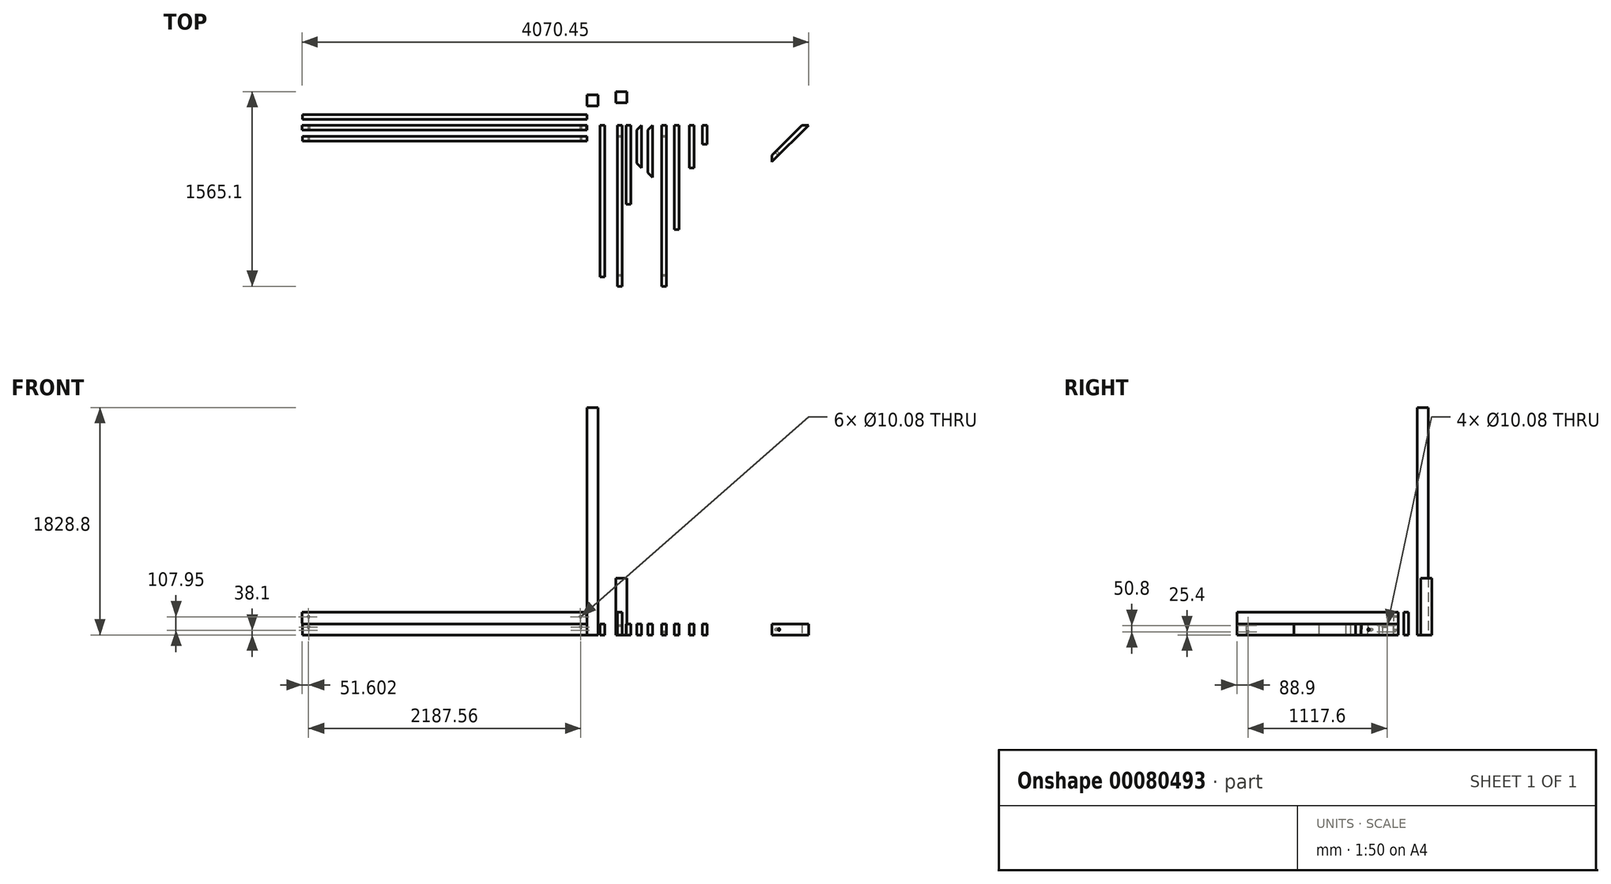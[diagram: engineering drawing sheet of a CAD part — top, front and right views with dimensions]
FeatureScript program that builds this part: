
annotation { "Feature Type Name" : "Feature", "Feature Type Description" : "" }
export const myFeature = defineFeature(function(context is Context, id is Id, definition is map)
    precondition{}
    {
        {
            var Q0;
            Q0=qCreatedBy(makeId("Right.planeOp"),FACE);
            var sketch = newSketch(context, id + "F0", { "sketchPlane" : qUnion([Q0])});
            skLineSegment(sketch, "E0.bottom", {"start": v(0, 0) * mm, "end": v(-38.1, 0) * mm});
            skLineSegment(sketch, "E0.top", {"start": v(0, 184.15) * mm, "end": v(-38.1, 184.15) * mm});
            skLineSegment(sketch, "E0.left", {"start": v(0, 0) * mm, "end": v(0, 184.15) * mm});
            skLineSegment(sketch, "E0.right", {"start": v(-38.1, 0) * mm, "end": v(-38.1, 184.15) * mm});
            skSolve(sketch);
        }
        {
            var Q0;
            Q0=makeQuery(id+"F0.imprint","IMPRINT",FACE,{"disambiguationData":[TD([[makeQuery(id+"F0.imprint","IMPRINT",EDGE,{"derivedFrom":sQuery(id+"F0.wireOp",EDGE,"E0.bottom")}),-1.0]])]});
            extrude(context, id + "F1", {"entities" : qUnion([Q0]), "oppositeDirection" : true, "depth" : 2289.96 * mm});
        }
        {
            var Q0;
            Q0=makeQuery(id+"F1.opExtrude","SWEPT_FACE",FACE,{"disambiguationData":[OSD([sQuery(id+"F0.wireOp",EDGE,"E0.right")])]});
            var sketch = newSketch(context, id + "F2", { "sketchPlane" : qUnion([Q0])});
            skLineSegment(sketch, "E1", {"start": v(0, 0) * mm, "end": v(0, 184.15) * mm});
            skLineSegment(sketch, "E2", {"start": v(0, 184.15) * mm, "end": v(-3.84, 184.15) * mm});
            skLineSegment(sketch, "E3", {"start": v(-3.84, 184.15) * mm, "end": v(0, 0) * mm});
            skLineSegment(sketch, "E4", {"start": v(-2289.96, 184.15) * mm, "end": v(-2286.13, 0) * mm});
            skLineSegment(sketch, "E5", {"start": v(-2286.13, 0) * mm, "end": v(-2289.96, 0) * mm});
            skLineSegment(sketch, "E6", {"start": v(-2289.96, 0) * mm, "end": v(-2289.96, 184.15) * mm});
            skSolve(sketch);
        }
        {
            var Q0;
            Q0 = qSketchRegion(id + "F2", true);
            extrude(context, id + "F3", {"entities" : qUnion([Q0]), "operationType" : NewBodyOperationType.REMOVE, "oppositeDirection" : true, "depth" : 38.1 * mm});
        }
        {
            var Q0;
            Q0=qCreatedBy(makeId("Front.planeOp"),FACE);
            var sketch = newSketch(context, id + "F4", { "sketchPlane" : qUnion([Q0])});
            skLineSegment(sketch, "E7.bottom", {"start": v(103.6, 0) * mm, "end": v(141.7, 0) * mm});
            skLineSegment(sketch, "E7.top", {"start": v(103.6, 88.9) * mm, "end": v(141.7, 88.9) * mm});
            skLineSegment(sketch, "E7.left", {"start": v(103.6, 0) * mm, "end": v(103.6, 88.9) * mm});
            skLineSegment(sketch, "E7.right", {"start": v(141.7, 0) * mm, "end": v(141.7, 88.9) * mm});
            skSolve(sketch);
        }
        {
            var Q0;
            Q0=makeQuery(id+"F4.imprint","IMPRINT",FACE,{"disambiguationData":[TD([[makeQuery(id+"F4.imprint","IMPRINT",EDGE,{"derivedFrom":sQuery(id+"F4.wireOp",EDGE,"E7.bottom")}),1.0]])]});
            extrude(context, id + "F5", {"entities" : qUnion([Q0]), "depth" : 1219.2 * mm});
        }
        {
            var Q0;
            Q0=qCreatedBy(makeId("Top.planeOp"),FACE);
            var sketch = newSketch(context, id + "F6", { "sketchPlane" : qUnion([Q0])});
            skLineSegment(sketch, "E8.bottom", {"start": v(0, 155.1) * mm, "end": v(88.9, 155.1) * mm});
            skLineSegment(sketch, "E8.top", {"start": v(0, 244) * mm, "end": v(88.9, 244) * mm});
            skLineSegment(sketch, "E8.left", {"start": v(0, 155.1) * mm, "end": v(0, 244) * mm});
            skLineSegment(sketch, "E8.right", {"start": v(88.9, 155.1) * mm, "end": v(88.9, 244) * mm});
            skSolve(sketch);
        }
        {
            var Q0;
            Q0 = qSketchRegion(id + "F6", true);
            extrude(context, id + "F7", {"entities" : qUnion([Q0]), "depth" : 1828.8 * mm});
        }
        {
            var Q0;
            Q0=qCreatedBy(makeId("Front.planeOp"),FACE);
            var sketch = newSketch(context, id + "F8", { "sketchPlane" : qUnion([Q0])});
            skLineSegment(sketch, "E9.bottom", {"start": v(244.55, 0) * mm, "end": v(282.65, 0) * mm});
            skLineSegment(sketch, "E9.top", {"start": v(244.55, 184.15) * mm, "end": v(282.65, 184.15) * mm});
            skLineSegment(sketch, "E9.left", {"start": v(244.55, 0) * mm, "end": v(244.55, 184.15) * mm});
            skLineSegment(sketch, "E9.right", {"start": v(282.65, 0) * mm, "end": v(282.65, 184.15) * mm});
            skSolve(sketch);
        }
        {
            var Q0;
            Q0=makeQuery(id+"F8.imprint","IMPRINT",FACE,{"disambiguationData":[TD([[makeQuery(id+"F8.imprint","IMPRINT",EDGE,{"derivedFrom":sQuery(id+"F8.wireOp",EDGE,"E9.bottom")}),1.0]])]});
            extrude(context, id + "F9", {"entities" : qUnion([Q0]), "depth" : 1295.4 * mm});
        }
        {
            var Q0;
            Q0=qCreatedBy(makeId("Front.planeOp"),FACE);
            var sketch = newSketch(context, id + "F10", { "sketchPlane" : qUnion([Q0])});
            skLineSegment(sketch, "E10.bottom", {"start": v(312.63, 0) * mm, "end": v(350.73, 0) * mm});
            skLineSegment(sketch, "E10.top", {"start": v(312.63, 88.9) * mm, "end": v(350.73, 88.9) * mm});
            skLineSegment(sketch, "E10.left", {"start": v(312.63, 0) * mm, "end": v(312.63, 88.9) * mm});
            skLineSegment(sketch, "E10.right", {"start": v(350.73, 0) * mm, "end": v(350.73, 88.9) * mm});
            skSolve(sketch);
        }
        {
            var Q0;
            Q0=makeQuery(id+"F10.imprint","IMPRINT",FACE,{"disambiguationData":[TD([[makeQuery(id+"F10.imprint","IMPRINT",EDGE,{"derivedFrom":sQuery(id+"F10.wireOp",EDGE,"E10.bottom")}),1.0]])]});
            extrude(context, id + "F11", {"entities" : qUnion([Q0]), "depth" : 635 * mm});
        }
        {
            var Q0;
            Q0=makeQuery(id+"F1.opExtrude","SWEPT_FACE",FACE,{"disambiguationData":[OSD([sQuery(id+"F0.wireOp",EDGE,"E0.right")])]});
            var sketch = newSketch(context, id + "F12", { "sketchPlane" : qUnion([Q0])});
            skPoint(sketch, "E11", {"position": v(-2238.36, 146.05) * mm});
            skPoint(sketch, "E12", {"position": v(-2236.1, 38.1) * mm});
            skPoint(sketch, "E13", {"position": v(-53.85, 146.05) * mm});
            skPoint(sketch, "E14", {"position": v(-51.6, 38.1) * mm});
            skSolve(sketch);
        }
        {
            var Q0;
            Q0=sQuery(id+"F12.wireOp",VERTEX,"E14");
            var Q1;
            Q1=sQuery(id+"F12.wireOp",VERTEX,"E13");
            var Q2;
            Q2=sQuery(id+"F12.wireOp",VERTEX,"E12");
            var Q3;
            Q3=sQuery(id+"F12.wireOp",VERTEX,"E11");
            var Q4;
            Q4=makeQuery(id+"F1.opExtrude","SWEPT_BODY",BODY,{"disambiguationData":[OSD([sQuery(id+"F0.wireOp",EDGE,"E0.bottom"),sQuery(id+"F0.wireOp",EDGE,"E0.top"),sQuery(id+"F0.wireOp",EDGE,"E0.left"),sQuery(id+"F0.wireOp",EDGE,"E0.right")])]});
            hole(context, id + "F13", {"style" : HoleStyle.SIMPLE, "endStyle" : HoleEndStyle.THROUGH, "standardTappedOrClearance" : lookupTablePath({ "standard" : "ANSI", "fit" : "Normal (ASME)", "size" : "3/8", "type" : "Clearance" }), "standardBlindInLast" : lookupTablePath({ "fit" : "Free", "standard" : "ANSI", "size" : "3/8", "type" : "Clearance" }), "holeDiameter" : 10.08 * mm, "locations" : qUnion([Q0, Q1, Q2, Q3]), "scope" : qUnion([Q4]), "isTappedThrough" : true});
        }
        {
            var Q0;
            Q0=makeQuery(id+"F9.opExtrude","SWEPT_FACE",FACE,{"disambiguationData":[OSD([sQuery(id+"F8.wireOp",EDGE,"E9.right")])]});
            var sketch = newSketch(context, id + "F14", { "sketchPlane" : qUnion([Q0])});
            skPoint(sketch, "E15", {"position": v(-1206.5, 76.2) * mm});
            skPoint(sketch, "E16", {"position": v(-88.9, 76.2) * mm});
            skSolve(sketch);
        }
        {
            var Q0;
            Q0=sQuery(id+"F14.wireOp",VERTEX,"4c446d8b-93f8-499f-88b7-25f558c8394a");
            var Q1;
            Q1=sQuery(id+"F14.wireOp",VERTEX,"E15");
            var Q2;
            Q2=sQuery(id+"F14.wireOp",VERTEX,"E16");
            var Q3;
            Q3=sQuery(id+"F14.wireOp",VERTEX,"ef1d34a0-cfd4-4a64-a352-8786edb42035");
            var Q4;
            Q4=makeQuery(id+"F9.opExtrude","SWEPT_BODY",BODY,{"disambiguationData":[OSD([sQuery(id+"F8.wireOp",EDGE,"E9.bottom"),sQuery(id+"F8.wireOp",EDGE,"E9.top"),sQuery(id+"F8.wireOp",EDGE,"E9.left"),sQuery(id+"F8.wireOp",EDGE,"E9.right")])]});
            hole(context, id + "F15", {"style" : HoleStyle.SIMPLE, "endStyle" : HoleEndStyle.THROUGH, "standardTappedOrClearance" : lookupTablePath({ "standard" : "ANSI", "fit" : "Normal (ASME)", "size" : "3/8", "type" : "Clearance" }), "standardBlindInLast" : lookupTablePath({ "fit" : "Free", "standard" : "ANSI", "size" : "3/8", "type" : "Clearance" }), "holeDiameter" : 10.08 * mm, "locations" : qUnion([Q0, Q1, Q2, Q3]), "scope" : qUnion([Q4]), "isTappedThrough" : true});
        }
        {
            var Q0;
            Q0=qCreatedBy(makeId("Front.planeOp"),FACE);
            var sketch = newSketch(context, id + "F16", { "sketchPlane" : qUnion([Q0])});
            skLineSegment(sketch, "E17.bottom", {"start": v(399.52, 0) * mm, "end": v(437.62, 0) * mm});
            skLineSegment(sketch, "E17.top", {"start": v(399.52, 88.9) * mm, "end": v(437.62, 88.9) * mm});
            skLineSegment(sketch, "E17.left", {"start": v(399.52, 0) * mm, "end": v(399.52, 88.9) * mm});
            skLineSegment(sketch, "E17.right", {"start": v(437.62, 0) * mm, "end": v(437.62, 88.9) * mm});
            skSolve(sketch);
        }
        {
            var Q0;
            Q0=makeQuery(id+"F16.imprint","IMPRINT",FACE,{"disambiguationData":[TD([[makeQuery(id+"F16.imprint","IMPRINT",EDGE,{"derivedFrom":sQuery(id+"F16.wireOp",EDGE,"E17.bottom")}),1.0]])]});
            extrude(context, id + "F17", {"entities" : qUnion([Q0]), "depth" : 342.9 * mm});
        }
        {
            var Q0;
            Q0=makeQuery(id+"F17.opExtrude","SWEPT_FACE",FACE,{"disambiguationData":[OSD([sQuery(id+"F16.wireOp",EDGE,"E17.top")])]});
            var sketch = newSketch(context, id + "F18", { "sketchPlane" : qUnion([Q0])});
            skLineSegment(sketch, "E18", {"start": v(437.62, 0) * mm, "end": v(399.52, -38.1) * mm});
            skLineSegment(sketch, "E19", {"start": v(399.52, -38.1) * mm, "end": v(399.52, 0) * mm});
            skLineSegment(sketch, "E20", {"start": v(399.52, 0) * mm, "end": v(437.62, 0) * mm});
            skLineSegment(sketch, "E21", {"start": v(437.62, -342.9) * mm, "end": v(399.52, -304.8) * mm});
            skLineSegment(sketch, "E22", {"start": v(399.52, -304.8) * mm, "end": v(399.52, -342.9) * mm});
            skLineSegment(sketch, "E23", {"start": v(399.52, -342.9) * mm, "end": v(437.62, -342.9) * mm});
            skSolve(sketch);
        }
        {
            var Q0;
            Q0=makeQuery(id+"F18.imprint","IMPRINT",FACE,{"disambiguationData":[TD([[makeQuery(id+"F18.imprint","IMPRINT",EDGE,{"derivedFrom":sQuery(id+"F18.wireOp",EDGE,"E18")}),-1.0]])]});
            var Q1;
            Q1=makeQuery(id+"F18.imprint","IMPRINT",FACE,{"disambiguationData":[TD([[makeQuery(id+"F18.imprint","IMPRINT",EDGE,{"derivedFrom":sQuery(id+"F18.wireOp",EDGE,"E21")}),1.0]])]});
            extrude(context, id + "F19", {"entities" : qUnion([Q0, Q1]), "operationType" : NewBodyOperationType.REMOVE, "oppositeDirection" : true, "depth" : 88.9 * mm});
        }
        {
            var Q0;
            Q0=qCreatedBy(makeId("Top.planeOp"),FACE);
            var sketch = newSketch(context, id + "F20", { "sketchPlane" : qUnion([Q0])});
            skLineSegment(sketch, "E24.bottom", {"start": v(230.08, 180.8) * mm, "end": v(318.98, 180.8) * mm});
            skLineSegment(sketch, "E24.top", {"start": v(230.08, 269.7) * mm, "end": v(318.98, 269.7) * mm});
            skLineSegment(sketch, "E24.left", {"start": v(230.08, 180.8) * mm, "end": v(230.08, 269.7) * mm});
            skLineSegment(sketch, "E24.right", {"start": v(318.98, 180.8) * mm, "end": v(318.98, 269.7) * mm});
            skSolve(sketch);
        }
        {
            var Q0;
            Q0=makeQuery(id+"F20.imprint","IMPRINT",FACE,{"disambiguationData":[TD([[makeQuery(id+"F20.imprint","IMPRINT",EDGE,{"derivedFrom":sQuery(id+"F20.wireOp",EDGE,"E24.bottom")}),1.0]])]});
            extrude(context, id + "F21", {"entities" : qUnion([Q0]), "depth" : 457.2 * mm});
        }
        {
            var Q0;
            Q0=qCreatedBy(makeId("Front.planeOp"),FACE);
            var sketch = newSketch(context, id + "F22", { "sketchPlane" : qUnion([Q0])});
            skLineSegment(sketch, "E25.bottom", {"start": v(487.43, 0) * mm, "end": v(525.53, 0) * mm});
            skLineSegment(sketch, "E25.top", {"start": v(487.43, 88.9) * mm, "end": v(525.53, 88.9) * mm});
            skLineSegment(sketch, "E25.left", {"start": v(487.43, 0) * mm, "end": v(487.43, 88.9) * mm});
            skLineSegment(sketch, "E25.right", {"start": v(525.53, 0) * mm, "end": v(525.53, 88.9) * mm});
            skSolve(sketch);
        }
        {
            var Q0;
            Q0=makeQuery(id+"F22.imprint","IMPRINT",FACE,{"disambiguationData":[TD([[makeQuery(id+"F22.imprint","IMPRINT",EDGE,{"derivedFrom":sQuery(id+"F22.wireOp",EDGE,"E25.bottom")}),1.0]])]});
            extrude(context, id + "F23", {"entities" : qUnion([Q0]), "depth" : 419.1 * mm});
        }
        {
            var Q0;
            Q0=makeQuery(id+"F23.opExtrude","SWEPT_FACE",FACE,{"disambiguationData":[OSD([sQuery(id+"F22.wireOp",EDGE,"E25.top")])]});
            var sketch = newSketch(context, id + "F24", { "sketchPlane" : qUnion([Q0])});
            skLineSegment(sketch, "E26", {"start": v(525.53, 0) * mm, "end": v(525.53, 38.1) * mm});
            skLineSegment(sketch, "E27", {"start": v(525.53, 38.1) * mm, "end": v(487.43, 0) * mm});
            skLineSegment(sketch, "E28", {"start": v(487.43, 0) * mm, "end": v(525.53, 0) * mm});
            skLineSegment(sketch, "E29", {"start": v(525.53, -419.1) * mm, "end": v(525.53, -457.2) * mm});
            skLineSegment(sketch, "E30", {"start": v(525.53, -457.2) * mm, "end": v(487.43, -419.1) * mm});
            skLineSegment(sketch, "E31", {"start": v(487.43, -419.1) * mm, "end": v(525.53, -419.1) * mm});
            skSolve(sketch);
        }
        {
            var Q0;
            Q0=makeQuery(id+"F24.imprint","IMPRINT",FACE,{"disambiguationData":[TD([[makeQuery(id+"F24.imprint","IMPRINT",EDGE,{"derivedFrom":sQuery(id+"F24.wireOp",EDGE,"E26")}),1.0]])]});
            var Q1;
            Q1=makeQuery(id+"F24.imprint","IMPRINT",FACE,{"disambiguationData":[TD([[makeQuery(id+"F24.imprint","IMPRINT",EDGE,{"derivedFrom":sQuery(id+"F24.wireOp",EDGE,"E29")}),-1.0]])]});
            extrude(context, id + "F25", {"entities" : qUnion([Q0, Q1]), "oppositeDirection" : true, "depth" : 88.9 * mm});
        }
        {
            var Q0;
            Q0=makeQuery(id+"F25.opExtrude","SWEPT_BODY",BODY,{"disambiguationData":[OSD([sQuery(id+"F24.wireOp",EDGE,"E29"),sQuery(id+"F24.wireOp",EDGE,"E30"),sQuery(id+"F24.wireOp",EDGE,"E31")])]});
            deleteBodies(context, id + "F26", {"entities" : qUnion([Q0])});
        }
        {
            var Q0;
            Q0=makeQuery(id+"F25.opExtrude","SWEPT_BODY",BODY,{"disambiguationData":[OSD([sQuery(id+"F24.wireOp",EDGE,"E26"),sQuery(id+"F24.wireOp",EDGE,"E27"),sQuery(id+"F24.wireOp",EDGE,"E28")])]});
            deleteBodies(context, id + "F27", {"entities" : qUnion([Q0])});
        }
        {
            var Q0;
            Q0=makeQuery(id+"F23.opExtrude","SWEPT_FACE",FACE,{"disambiguationData":[OSD([sQuery(id+"F22.wireOp",EDGE,"E25.top")])]});
            var sketch = newSketch(context, id + "F28", { "sketchPlane" : qUnion([Q0])});
            skLineSegment(sketch, "E32", {"start": v(525.53, 0) * mm, "end": v(487.43, -38.1) * mm});
            skLineSegment(sketch, "E33", {"start": v(487.43, -38.1) * mm, "end": v(487.43, 0) * mm});
            skLineSegment(sketch, "E34", {"start": v(487.43, 0) * mm, "end": v(525.53, 0) * mm});
            skLineSegment(sketch, "E35", {"start": v(525.53, -419.1) * mm, "end": v(487.43, -381) * mm});
            skLineSegment(sketch, "E36", {"start": v(487.43, -381) * mm, "end": v(487.43, -419.1) * mm});
            skLineSegment(sketch, "E37", {"start": v(487.43, -419.1) * mm, "end": v(525.53, -419.1) * mm});
            skSolve(sketch);
        }
        {
            var Q0;
            Q0=makeQuery(id+"F28.imprint","IMPRINT",FACE,{"disambiguationData":[TD([[makeQuery(id+"F28.imprint","IMPRINT",EDGE,{"derivedFrom":sQuery(id+"F28.wireOp",EDGE,"E32")}),-1.0]])]});
            var Q1;
            Q1=makeQuery(id+"F28.imprint","IMPRINT",FACE,{"disambiguationData":[TD([[makeQuery(id+"F28.imprint","IMPRINT",EDGE,{"derivedFrom":sQuery(id+"F28.wireOp",EDGE,"E35")}),1.0]])]});
            extrude(context, id + "F29", {"entities" : qUnion([Q0, Q1]), "operationType" : NewBodyOperationType.REMOVE, "oppositeDirection" : true, "depth" : 88.9 * mm});
        }
        {
            var Q0;
            Q0=qCreatedBy(makeId("Right.planeOp"),FACE);
            var sketch = newSketch(context, id + "F30", { "sketchPlane" : qUnion([Q0])});
            skLineSegment(sketch, "E38.bottom", {"start": v(-88.17, 0) * mm, "end": v(-126.27, 0) * mm});
            skLineSegment(sketch, "E38.top", {"start": v(-88.17, 88.9) * mm, "end": v(-126.27, 88.9) * mm});
            skLineSegment(sketch, "E38.left", {"start": v(-88.17, 0) * mm, "end": v(-88.17, 88.9) * mm});
            skLineSegment(sketch, "E38.right", {"start": v(-126.27, 0) * mm, "end": v(-126.27, 88.9) * mm});
            skSolve(sketch);
        }
        {
            var Q0;
            Q0=makeQuery(id+"F30.imprint","IMPRINT",FACE,{"disambiguationData":[TD([[makeQuery(id+"F30.imprint","IMPRINT",EDGE,{"derivedFrom":sQuery(id+"F30.wireOp",EDGE,"E38.bottom")}),-1.0]])]});
            extrude(context, id + "F31", {"entities" : qUnion([Q0]), "oppositeDirection" : true, "depth" : 2287.9 * mm});
        }
        {
            var Q0;
            Q0=makeQuery(id+"F31.opExtrude","SWEPT_FACE",FACE,{"disambiguationData":[OSD([sQuery(id+"F30.wireOp",EDGE,"E38.right")])]});
            var sketch = newSketch(context, id + "F32", { "sketchPlane" : qUnion([Q0])});
            skLineSegment(sketch, "E39", {"start": v(0, 0) * mm, "end": v(-1.85, 88.9) * mm});
            skLineSegment(sketch, "E40", {"start": v(-1.85, 88.9) * mm, "end": v(0, 88.9) * mm});
            skLineSegment(sketch, "E41", {"start": v(0, 88.9) * mm, "end": v(0, 0) * mm});
            skLineSegment(sketch, "E42", {"start": v(-2287.91, 88.9) * mm, "end": v(-2286.06, 0) * mm});
            skLineSegment(sketch, "E43", {"start": v(-2286.06, 0) * mm, "end": v(-2287.91, 0) * mm});
            skLineSegment(sketch, "E44", {"start": v(-2287.91, 0) * mm, "end": v(-2287.91, 88.9) * mm});
            skSolve(sketch);
        }
        {
            var Q0;
            Q0=makeQuery(id+"F32.imprint","IMPRINT",FACE,{"disambiguationData":[TD([[makeQuery(id+"F32.imprint","IMPRINT",EDGE,{"derivedFrom":sQuery(id+"F32.wireOp",EDGE,"E42")}),-1.0]])]});
            var Q1;
            Q1=makeQuery(id+"F32.imprint","IMPRINT",FACE,{"disambiguationData":[TD([[makeQuery(id+"F32.imprint","IMPRINT",EDGE,{"derivedFrom":sQuery(id+"F32.wireOp",EDGE,"E39")}),-1.0]])]});
            extrude(context, id + "F33", {"entities" : qUnion([Q0, Q1]), "operationType" : NewBodyOperationType.REMOVE, "oppositeDirection" : true, "depth" : 38.1 * mm});
        }
        {
            var Q0;
            Q0=qCreatedBy(makeId("Front.planeOp"),FACE);
            var sketch = newSketch(context, id + "F34", { "sketchPlane" : qUnion([Q0])});
            skLineSegment(sketch, "E45.bottom", {"start": v(600.5, 0) * mm, "end": v(638.6, 0) * mm});
            skLineSegment(sketch, "E45.top", {"start": v(600.5, 88.9) * mm, "end": v(638.6, 88.9) * mm});
            skLineSegment(sketch, "E45.left", {"start": v(600.5, 0) * mm, "end": v(600.5, 88.9) * mm});
            skLineSegment(sketch, "E45.right", {"start": v(638.6, 0) * mm, "end": v(638.6, 88.9) * mm});
            skSolve(sketch);
        }
        {
            var Q0;
            Q0=makeQuery(id+"F34.imprint","IMPRINT",FACE,{"disambiguationData":[TD([[makeQuery(id+"F34.imprint","IMPRINT",EDGE,{"derivedFrom":sQuery(id+"F34.wireOp",EDGE,"E45.bottom")}),1.0]])]});
            extrude(context, id + "F35", {"entities" : qUnion([Q0]), "depth" : 1295.4 * mm});
        }
        {
            var Q0;
            Q0=makeQuery(id+"F31.opExtrude","SWEPT_FACE",FACE,{"disambiguationData":[OSD([sQuery(id+"F30.wireOp",EDGE,"E38.right")])]});
            var sketch = newSketch(context, id + "F36", { "sketchPlane" : qUnion([Q0])});
            skPoint(sketch, "E46", {"position": v(-2237.11, 63.5) * mm});
            skPoint(sketch, "E47", {"position": v(-50.8, 63.5) * mm});
            skSolve(sketch);
        }
        {
            var Q0;
            Q0=sQuery(id+"F36.wireOp",VERTEX,"E46");
            var Q1;
            Q1=sQuery(id+"F36.wireOp",VERTEX,"E47");
            var Q2;
            Q2=makeQuery(id+"F31.opExtrude","SWEPT_BODY",BODY,{"disambiguationData":[OSD([sQuery(id+"F30.wireOp",EDGE,"E38.bottom"),sQuery(id+"F30.wireOp",EDGE,"E38.top"),sQuery(id+"F30.wireOp",EDGE,"E38.left"),sQuery(id+"F30.wireOp",EDGE,"E38.right")])]});
            hole(context, id + "F37", {"style" : HoleStyle.SIMPLE, "endStyle" : HoleEndStyle.THROUGH, "standardTappedOrClearance" : lookupTablePath({ "standard" : "ANSI", "fit" : "Normal (ASME)", "size" : "3/8", "type" : "Clearance" }), "standardBlindInLast" : lookupTablePath({ "fit" : "Free", "standard" : "ANSI", "size" : "3/8", "type" : "Clearance" }), "holeDiameter" : 10.08 * mm, "locations" : qUnion([Q0, Q1]), "scope" : qUnion([Q2]), "isTappedThrough" : true});
        }
        {
            var Q0;
            Q0=makeQuery(id+"F35.opExtrude","SWEPT_FACE",FACE,{"disambiguationData":[OSD([sQuery(id+"F34.wireOp",EDGE,"E45.right")])]});
            var sketch = newSketch(context, id + "F38", { "sketchPlane" : qUnion([Q0])});
            skPoint(sketch, "E48", {"position": v(-1206.5, 25.4) * mm});
            skPoint(sketch, "E49", {"position": v(-88.9, 25.4) * mm});
            skSolve(sketch);
        }
        {
            var Q0;
            Q0=sQuery(id+"F38.wireOp",VERTEX,"E49");
            var Q1;
            Q1=sQuery(id+"F38.wireOp",VERTEX,"E48");
            var Q2;
            Q2=makeQuery(id+"F35.opExtrude","SWEPT_BODY",BODY,{"disambiguationData":[OSD([sQuery(id+"F34.wireOp",EDGE,"E45.bottom"),sQuery(id+"F34.wireOp",EDGE,"E45.top"),sQuery(id+"F34.wireOp",EDGE,"E45.left"),sQuery(id+"F34.wireOp",EDGE,"E45.right")])]});
            hole(context, id + "F39", {"style" : HoleStyle.SIMPLE, "endStyle" : HoleEndStyle.THROUGH, "standardTappedOrClearance" : lookupTablePath({ "standard" : "ANSI", "fit" : "Normal (ASME)", "size" : "3/8", "type" : "Clearance" }), "standardBlindInLast" : lookupTablePath({ "fit" : "Free", "standard" : "ANSI", "size" : "3/8", "type" : "Clearance" }), "holeDiameter" : 10.08 * mm, "locations" : qUnion([Q0, Q1]), "scope" : qUnion([Q2]), "isTappedThrough" : true});
        }
        {
            var Q0;
            Q0=qCreatedBy(makeId("Front.planeOp"),FACE);
            var sketch = newSketch(context, id + "F40", { "sketchPlane" : qUnion([Q0])});
            skLineSegment(sketch, "E50.bottom", {"start": v(700.78, 0) * mm, "end": v(738.88, 0) * mm});
            skLineSegment(sketch, "E50.top", {"start": v(700.78, 88.9) * mm, "end": v(738.88, 88.9) * mm});
            skLineSegment(sketch, "E50.left", {"start": v(700.78, 0) * mm, "end": v(700.78, 88.9) * mm});
            skLineSegment(sketch, "E50.right", {"start": v(738.88, 0) * mm, "end": v(738.88, 88.9) * mm});
            skSolve(sketch);
        }
        {
            var Q0;
            Q0=makeQuery(id+"F40.imprint","IMPRINT",FACE,{"disambiguationData":[TD([[makeQuery(id+"F40.imprint","IMPRINT",EDGE,{"derivedFrom":sQuery(id+"F40.wireOp",EDGE,"E50.bottom")}),1.0]])]});
            extrude(context, id + "F41", {"entities" : qUnion([Q0]), "depth" : 838.2 * mm});
        }
        {
            var Q0;
            Q0=qCreatedBy(makeId("Front.planeOp"),FACE);
            var sketch = newSketch(context, id + "F42", { "sketchPlane" : qUnion([Q0])});
            skLineSegment(sketch, "E51.bottom", {"start": v(821.33, 88.9) * mm, "end": v(859.43, 88.9) * mm});
            skLineSegment(sketch, "E51.top", {"start": v(821.33, 0) * mm, "end": v(859.43, 0) * mm});
            skLineSegment(sketch, "E51.left", {"start": v(821.33, 88.9) * mm, "end": v(821.33, 0) * mm});
            skLineSegment(sketch, "E51.right", {"start": v(859.43, 88.9) * mm, "end": v(859.43, 0) * mm});
            skSolve(sketch);
        }
        {
            var Q0;
            Q0=makeQuery(id+"F42.imprint","IMPRINT",FACE,{"disambiguationData":[TD([[makeQuery(id+"F42.imprint","IMPRINT",EDGE,{"derivedFrom":sQuery(id+"F42.wireOp",EDGE,"E51.bottom")}),-1.0]])]});
            extrude(context, id + "F43", {"entities" : qUnion([Q0]), "depth" : 342.9 * mm});
        }
        {
            var Q0;
            Q0=makeQuery(id+"F43.opExtrude","SWEPT_FACE",FACE,{"disambiguationData":[OSD([sQuery(id+"F42.wireOp",EDGE,"E51.right")])]});
            var sketch = newSketch(context, id + "F44", { "sketchPlane" : qUnion([Q0])});
            skLineSegment(sketch, "E52", {"start": v(-342.9, 88.9) * mm, "end": v(-341.04, 0) * mm});
            skLineSegment(sketch, "E53", {"start": v(-341.04, 0) * mm, "end": v(-342.9, 0) * mm});
            skLineSegment(sketch, "E54", {"start": v(-342.9, 0) * mm, "end": v(-342.9, 88.9) * mm});
            skSolve(sketch);
        }
        {
            var Q0;
            Q0=makeQuery(id+"F44.imprint","IMPRINT",FACE,{"disambiguationData":[TD([[makeQuery(id+"F44.imprint","IMPRINT",EDGE,{"derivedFrom":sQuery(id+"F44.wireOp",EDGE,"E52")}),-1.0]])]});
            extrude(context, id + "F45", {"entities" : qUnion([Q0]), "operationType" : NewBodyOperationType.REMOVE, "oppositeDirection" : true, "depth" : 38.1 * mm});
        }
        {
            var Q0;
            Q0=qCreatedBy(makeId("Front.planeOp"),FACE);
            var sketch = newSketch(context, id + "F46", { "sketchPlane" : qUnion([Q0])});
            skLineSegment(sketch, "E55.bottom", {"start": v(926.3, 0) * mm, "end": v(964.4, 0) * mm});
            skLineSegment(sketch, "E55.top", {"start": v(926.3, 88.9) * mm, "end": v(964.4, 88.9) * mm});
            skLineSegment(sketch, "E55.left", {"start": v(926.3, 0) * mm, "end": v(926.3, 88.9) * mm});
            skLineSegment(sketch, "E55.right", {"start": v(964.4, 0) * mm, "end": v(964.4, 88.9) * mm});
            skSolve(sketch);
        }
        {
            var Q0;
            Q0=makeQuery(id+"F46.imprint","IMPRINT",FACE,{"disambiguationData":[TD([[makeQuery(id+"F46.imprint","IMPRINT",EDGE,{"derivedFrom":sQuery(id+"F46.wireOp",EDGE,"E55.bottom")}),1.0]])]});
            extrude(context, id + "F47", {"entities" : qUnion([Q0]), "depth" : 152.4 * mm});
        }
        {
            var Q0;
            Q0=qCreatedBy(makeId("Top.planeOp"),FACE);
            var sketch = newSketch(context, id + "F48", { "sketchPlane" : qUnion([Q0])});
            skLineSegment(sketch, "E56", {"start": v(1780.5, 0) * mm, "end": v(1726.6, 0) * mm});
            skLineSegment(sketch, "E57", {"start": v(1726.6, 0) * mm, "end": v(1484.14, -242.47) * mm});
            skLineSegment(sketch, "E58", {"start": v(1484.14, -242.47) * mm, "end": v(1484.14, -296.35) * mm});
            skLineSegment(sketch, "E59", {"start": v(1484.14, -296.35) * mm, "end": v(1780.5, 0) * mm});
            skSolve(sketch);
        }
        {
            var Q0;
            Q0=makeQuery(id+"F48.imprint","IMPRINT",FACE,{"disambiguationData":[TD([[makeQuery(id+"F48.imprint","IMPRINT",EDGE,{"derivedFrom":sQuery(id+"F48.wireOp",EDGE,"E56")}),1.0]])]});
            extrude(context, id + "F49", {"entities" : qUnion([Q0]), "depth" : 88.9 * mm});
        }
        {
            var Q0;
            Q0=qCreatedBy(makeId("Front.planeOp"),FACE);
            var sketch = newSketch(context, id + "F50", { "sketchPlane" : qUnion([Q0])});
            skLineSegment(sketch, "E60", {"start": v(1484.14, 0) * mm, "end": v(1484.14, 89.06) * mm});
            skLineSegment(sketch, "E61", {"start": v(1484.14, 89.06) * mm, "end": v(1486, 89.06) * mm});
            skLineSegment(sketch, "E62", {"start": v(1486, 89.06) * mm, "end": v(1484.14, 0) * mm});
            skSolve(sketch);
        }
        {
            var Q0;
            Q0=makeQuery(id+"F50.imprint","IMPRINT",FACE,{"disambiguationData":[TD([[makeQuery(id+"F50.imprint","IMPRINT",EDGE,{"derivedFrom":sQuery(id+"F50.wireOp",EDGE,"E60")}),-1.0]])]});
            extrude(context, id + "F51", {"entities" : qUnion([Q0]), "operationType" : NewBodyOperationType.REMOVE, "depth" : 508 * mm});
        }
        {
            var Q0;
            Q0=makeQuery(id+"F49.opExtrude","SWEPT_FACE",FACE,{"disambiguationData":[OSD([sQuery(id+"F48.wireOp",EDGE,"E57")])]});
            var sketch = newSketch(context, id + "F52", { "sketchPlane" : qUnion([Q0])});
            skCircle(sketch, "E63", {"center": v(-922.82, 43.84) * mm, "radius": 9.14 * mm});
            skSolve(sketch);
        }
        {
            var Q0;
            Q0=makeQuery(id+"F52.imprint","IMPRINT",FACE,{"disambiguationData":[TD([[makeQuery(id+"F52.imprint","IMPRINT",EDGE,{"derivedFrom":sQuery(id+"F52.wireOp",EDGE,"E63")}),1.0]])]});
            extrude(context, id + "F53", {"entities" : qUnion([Q0]), "operationType" : NewBodyOperationType.REMOVE, "oppositeDirection" : true, "depth" : 38.1 * mm});
        }
        {
            var Q0;
            Q0=qCreatedBy(makeId("Right.planeOp"),FACE);
            var sketch = newSketch(context, id + "F54", { "sketchPlane" : qUnion([Q0])});
            skLineSegment(sketch, "E64.bottom", {"start": v(45.95, 0) * mm, "end": v(84.05, 0) * mm});
            skLineSegment(sketch, "E64.top", {"start": v(45.95, 184.15) * mm, "end": v(84.05, 184.15) * mm});
            skLineSegment(sketch, "E64.left", {"start": v(45.95, 0) * mm, "end": v(45.95, 184.15) * mm});
            skLineSegment(sketch, "E64.right", {"start": v(84.05, 0) * mm, "end": v(84.05, 184.15) * mm});
            skSolve(sketch);
        }
        {
            var Q0;
            Q0 = qSketchRegion(id + "F54", true);
            extrude(context, id + "F55", {"entities" : qUnion([Q0]), "oppositeDirection" : true, "depth" : 2286 * mm});
        }
    });
